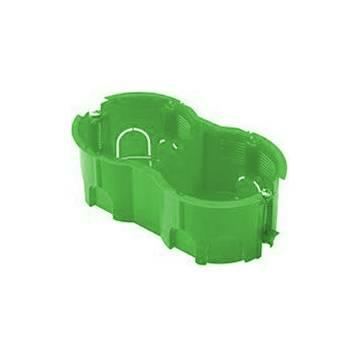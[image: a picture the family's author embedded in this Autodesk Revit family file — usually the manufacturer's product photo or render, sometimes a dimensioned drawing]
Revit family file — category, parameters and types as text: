
# Revit family: Building-FlushMountingEnclosures-GEWISS-24SC-GREENWALL-BOXES_ROUND_DOUBLE
name_source: partatom
category: Apparecchi elettrici
revit_build: Autodesk Revit 2016 (Build: 20161004_0715(x64)
units: mm (PartAtom-declared; Revit-internal decimal feet)

## family parameters
Condiviso = Sì
Host = Superficie
Mantenere orientamento annotazione = Sì
Numero OmniClass = 23.80.30.14.24
Punto di calcolo locali = Sì
Quota connettore circolare = Usa diametro
Taglio con vuoti quando caricato = Sì
Tipo di parte = Normale
Titolo OmniClass = Junction Boxes

## types (1)
- GW24282PM - Halogen free - 125x72x45
    Carico apparente = 0 VA
    Catalogue = BUILDING
    Catalogue Range = 24SC
    Characteristics = Halogen free
    Classificazione = Altro
    Description: = Double
    Descrizione = PLASTERBOARD W. DOUBLE ROUND BOX - GW
    Dimensions (mm) = 125x72x45
    EAN code = 8011564802032
    Electrocod = 0210
    For walls = Plasterboard
    Glow Wire Test = 850°C
    IDF = 2ec72f55-efe3-4be1-84a6-3bc7228eb656
    IDT = 5e032acf-9e89-4430-9960-546520e20b75
    IP degree = IP40
    Immagine tipo = GW24282PM.jpg
    Installation = Flush mounting enclosures
    Metallo = GEWISS - Elementi acciaio
    Modello = GW24282PM
    Operating temperature = -15 ÷ +60°C
    Plate centre distance Chorus International = 57MM
    Produttore = GEWISS S.p.A.
    Profondità = 45 mm  [stored 0.147638 ft]
    Prospetto di default = 1219.2 mm
    SEO = Box
    Scatola = GEWISS - scatola a incasso
    Shock resistance = IK07
    Technical sheet = https://www.gewiss.com
    Thermo-pressure with ball = 70
    Type of material = Halogen-free in compliance with EN 60754-2
    URL = https://www.gewiss.com
    Version file RFA = 19.0
    Voltaggio = 0 V

note: source unit labels omitted for Thermo-pressure with ball — the stored unit's dimension contradicts the parameter name (converter mislabeling)

note: [stored X ft] marks values corroborated as IEEE doubles in the binary element streams (Revit-internal decimal feet)

## geometry (parser evidence)
native form markers: Sweep x2
no freeform markers — native parametric forms only
